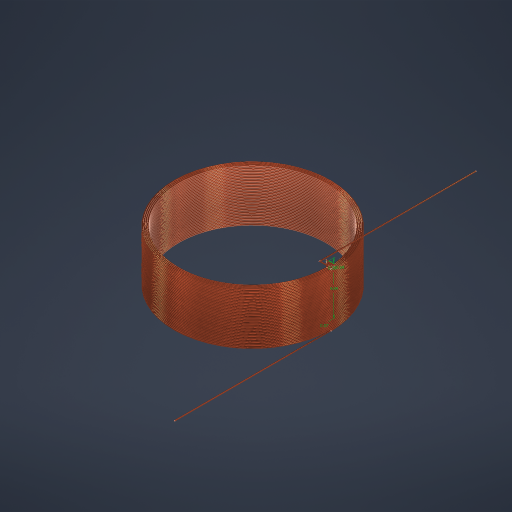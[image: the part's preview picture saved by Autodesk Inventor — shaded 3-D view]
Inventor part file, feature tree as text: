
AUTODESK INVENTOR PART (.ipt)
format: ipt  version: 2024.2 (Build 282272000, 272)  size: 3,825,152 bytes
history: native  units: mm
features: sketch x9, other x8, chamfer x8, sweep x4, extrude x1
ambient origin geometry x8: Origin, YZ Plane, XZ Plane, XY Plane, X Axis, Y Axis, Z Axis, Center Point
bodies: Volumenkörper1 (feature_tree), Volumenkörper2 (feature_tree), Volumenkörper3 (feature_tree), Volumenkörper4 (feature_tree), Volumenkörper5 (feature_tree), Volumenkörper6 (feature_tree), Volumenkörper7 (feature_tree), Volumenkörper8 (feature_tree)
feature tree (30):
  other  "Spirale1"
  other  "Spirale2"
  other  "Spirale3"
  other  "Spirale4"
  sweep  "Sweeping1"
  other  "3D-Skizze7"
  sketch  "Skizze15"  dims[d26=0.101mm d27=4.0mm d28=400.0mm d29=0.0mm d30=90.0deg d31=90.0deg d32=0.0mm d33=0.0mm]
  sweep  "Sweeping2"
  sweep  "Sweeping3"
  chamfer  "Fasen4"  Distance=0.7mm
  chamfer  "Fasen5"  [1 undecoded]
  chamfer  "Fasen6"  Distance=0.39mm
  chamfer  "Fasen7"  Distance=0.59mm
  chamfer  "Fasen8"  Distance=4.04mm
  chamfer  "Fasen9"  Distance=0.57mm
  extrude  "Extrusion1"  TaperAngle=0.0deg  [1 undecoded]
  chamfer  "Fasen10"  Distance=0.37mm
  sweep  "Sweeping4"
  chamfer  "Fasen11"  Distance=0.33mm
  sketch  "Skizze1"  dims[d0=0.1mm d1=6.0mm]
  other  "3D-Skizze5"
  sketch  "Skizze14"  dims[d16=0.1mm d17=5.6995mm d18=0.101mm d19=4.0mm d20=400.0mm d21=0.0mm d22=90.0deg d23=90.0deg d24=0.0mm d25=0.0mm]
  sketch  "Skizze16"  dims[d34=0.101mm d35=4.0mm d36=400.0mm d37=0.0mm d38=90.0deg d39=90.0deg d40=0.0mm d41=0.0mm d45=0.5mm]
  other  "3D-Skizze8"
  sketch  "Skizze17"  dims[d46=0.8mm]
  sketch  "Skizze18"  dims[d47=4.04mm]
  other  "3D-Skizze9"
  sketch  "Skizze19"  dims[d48=0.8mm d49=0.7mm d50=0.0mm d51=0.0mm d57=0.39mm d58=0.59mm d59=4.04mm d60=0.57mm d61=0.0mm d62=0.0mm d65=0.37mm d66=4.04mm d67=0.33mm d68=0.27mm d69=0.0mm d70=0.0mm d71=0.08mm d72=0.08mm d73=0.08mm d83=0.01mm d84=2.0mm d85=45.0deg d86=0.01mm d87=2.0mm d88=45.0deg d89=0.01mm d90=2.0mm d91=45.0deg d92=0.01mm d93=2.0mm d94=45.0deg d95=0.01mm d96=2.0mm d97=45.0deg d98=0.01mm d99=2.0mm d100=45.0deg d101=0.08mm d102=12.0mm d103=0.0mm d104=0.01mm d105=2.0mm d106=45.0deg d107=0.17mm d108=0.7mm d109=12.0mm d110=0.08mm d111=0.0mm d112=0.0mm d113=0.01mm d114=2.0mm d115=45.0deg]
  sketch  "Skizze3"  dims[d2=0.101mm d3=4.0mm d4=400.0mm d5=0.0mm d6=0.0mm d7=90.0deg d8=0.0mm d9=0.0mm d12=0.1mm d13=5.8995mm]
  sketch  "Skizze4"  dims[d14=0.1mm d15=5.7995mm]
note: 2 required parameter values undecoded (feature->parameter linkage not recoverable at this tier; creation-order binding heuristic only, values carry confidence <= 0.55)
